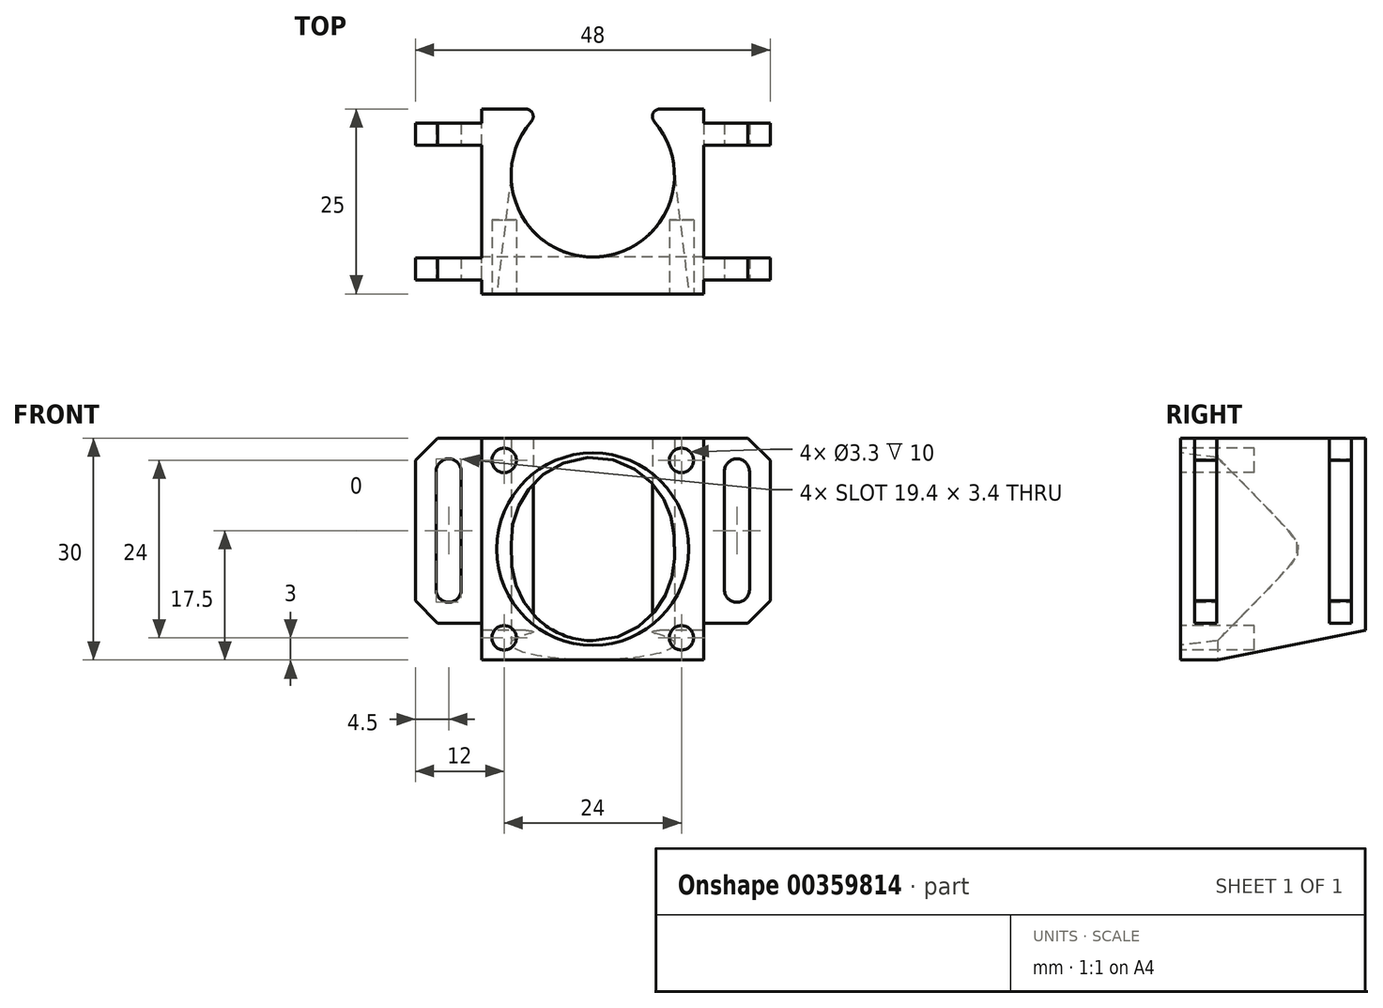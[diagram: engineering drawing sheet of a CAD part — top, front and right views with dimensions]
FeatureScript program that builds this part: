
annotation { "Feature Type Name" : "Feature", "Feature Type Description" : "" }
export const myFeature = defineFeature(function(context is Context, id is Id, definition is map)
    precondition{}
    {
        {
            var Q0;
            Q0=qCreatedBy(makeId("Top.planeOp"),FACE);
            var sketch = newSketch(context, id + "F0", { "sketchPlane" : qUnion([Q0])});
            skLineSegment(sketch, "E0.bottom", {"start": v(0, 0) * mm, "end": v(30, 0) * mm});
            skLineSegment(sketch, "E0.top", {"start": v(0, 25) * mm, "end": v(8.52, 25) * mm});
            skLineSegment(sketch, "E0.left", {"start": v(0, 0) * mm, "end": v(0, 25) * mm});
            skLineSegment(sketch, "E0.right", {"start": v(30, 0) * mm, "end": v(30, 25) * mm});
            skArc(sketch, "E1", {"start": v(8.52, 25) * mm, "mid": v(15, 5) * mm, "end": v(21.48, 25) * mm});
            skPoint(sketch, "E1.centerSnap0", {"position": v(15, 25) * mm});
            skLineSegment(sketch, "E2.trimOffspring", {"start": v(21.48, 25) * mm, "end": v(30, 25) * mm});
            skSolve(sketch);
        }
        {
            var Q0;
            Q0 = qSketchRegion(id + "F0", true);
            extrude(context, id + "F1", {"entities" : qUnion([Q0]), "depth" : 30 * mm});
        }
        {
            var Q0;
            Q0=makeQuery(id+"F1.opExtrude","SWEPT_FACE",FACE,{"disambiguationData":[OSD([sQuery(id+"F0.wireOp",EDGE,"E0.left")])]});
            var sketch = newSketch(context, id + "F2", { "sketchPlane" : qUnion([Q0])});
            skLineSegment(sketch, "E3", {"start": v(-25, 4) * mm, "end": v(-5, 0) * mm});
            skLineSegment(sketch, "E4", {"start": v(-5, 0) * mm, "end": v(-25, 0) * mm});
            skLineSegment(sketch, "E5", {"start": v(-25, 0) * mm, "end": v(-25, 4) * mm});
            skSolve(sketch);
        }
        {
            var Q0;
            Q0=makeQuery(id+"F2.imprint","IMPRINT",FACE,{"disambiguationData":[TD([[makeQuery(id+"F2.imprint","IMPRINT",EDGE,{"derivedFrom":sQuery(id+"F2.wireOp",EDGE,"E3")}),-1.0]])]});
            extrude(context, id + "F3", {"entities" : qUnion([Q0]), "operationType" : NewBodyOperationType.REMOVE, "endBound" : BoundingType.THROUGH_ALL, "oppositeDirection" : true, "depth" : 25 * mm});
        }
        {
            var Q0;
            Q0=makeQuery(id+"F1.opExtrude","CAP_FACE",FACE,{"disambiguationData":[OSD([sQuery(id+"F0.wireOp",EDGE,"E0.bottom"),sQuery(id+"F0.wireOp",EDGE,"E0.top"),sQuery(id+"F0.wireOp",EDGE,"E0.left"),sQuery(id+"F0.wireOp",EDGE,"E0.right"),sQuery(id+"F0.wireOp",EDGE,"E1"),sQuery(id+"F0.wireOp",EDGE,"E2.trimOffspring")])],"isStart":false});
            cPlane(context, id + "F4", {"entities" : qUnion([Q0]), "cplaneType" : CPlaneType.OFFSET, "offset" : 15 * mm, "oppositeDirection" : true, "width" : 150 * mm, "height" : 150 * mm});
        }
        {
            var Q0;
            Q0=qCreatedBy(id+"F4.planeOp",FACE);
            var sketch = newSketch(context, id + "F5", { "sketchPlane" : qUnion([Q0])});
            skArc(sketch, "E6.0.0", {"start": v(15, 5) * mm, "mid": v(7.19, 8.24) * mm, "end": v(3.95, 16.05) * mm});
            skLineSegment(sketch, "E6.0.1", {"start": v(8.52, 25) * mm, "end": v(0, 25) * mm, "construction": true});
            skLineSegment(sketch, "E6.0.2", {"start": v(0, 25) * mm, "end": v(0, 0) * mm, "construction": true});
            skLineSegment(sketch, "E6.0.3", {"start": v(0, 0) * mm, "end": v(30, 0) * mm, "construction": true});
            skLineSegment(sketch, "E6.0.4", {"start": v(30, 0) * mm, "end": v(30, 25) * mm, "construction": true});
            skLineSegment(sketch, "E6.0.5", {"start": v(30, 25) * mm, "end": v(21.48, 25) * mm, "construction": true});
            skLineSegment(sketch, "E7", {"start": v(3.95, 16.05) * mm, "end": v(2, 0) * mm});
            skLineSegment(sketch, "E8", {"start": v(2, 0) * mm, "end": v(15, 0) * mm});
            skLineSegment(sketch, "E9", {"start": v(15, 0) * mm, "end": v(15, 5) * mm});
            skLineSegment(sketch, "E10", {"start": v(15, 16.05) * mm, "end": v(15, 5) * mm, "construction": true});
            skSolve(sketch);
        }
        {
            var Q0;
            Q0 = qSketchRegion(id + "F5", true);
            var Q1;
            Q1=sQuery(id+"F5.wireOp",EDGE,"E10");
            revolve(context, id + "F6", {"operationType" : NewBodyOperationType.REMOVE, "entities" : qUnion([Q0]), "axis" : qUnion([Q1]), "revolveType" : RevolveType.FULL, "oppositeDirection" : true});
        }
        {
            var Q0;
            Q0=makeQuery(id+"F1.opExtrude","SWEPT_FACE",FACE,{"disambiguationData":[OSD([sQuery(id+"F0.wireOp",EDGE,"E0.bottom")])]});
            var sketch = newSketch(context, id + "F7", { "sketchPlane" : qUnion([Q0])});
            skCircle(sketch, "E11", {"center": v(3, 27) * mm, "radius": 1.65 * mm});
            skCircle(sketch, "E12", {"center": v(27, 27) * mm, "radius": 1.65 * mm});
            skCircle(sketch, "E13", {"center": v(27, 3) * mm, "radius": 1.65 * mm});
            skCircle(sketch, "E14", {"center": v(3, 3) * mm, "radius": 1.65 * mm});
            skSolve(sketch);
        }
        {
            var Q0;
            Q0 = qSketchRegion(id + "F7", true);
            extrude(context, id + "F8", {"entities" : qUnion([Q0]), "operationType" : NewBodyOperationType.REMOVE, "oppositeDirection" : true, "depth" : 10 * mm});
        }
        {
            var Q0;
            Q0=makeQuery(id+"F1.opExtrude","SWEPT_FACE",FACE,{"disambiguationData":[OSD([sQuery(id+"F0.wireOp",EDGE,"E0.right")])]});
            var sketch = newSketch(context, id + "F9", { "sketchPlane" : qUnion([Q0])});
            skLineSegment(sketch, "E15.bottom", {"start": v(1.9, 30) * mm, "end": v(4.9, 30) * mm});
            skLineSegment(sketch, "E15.top", {"start": v(1.9, 5) * mm, "end": v(4.9, 5) * mm});
            skLineSegment(sketch, "E15.left", {"start": v(1.9, 30) * mm, "end": v(1.9, 5) * mm});
            skLineSegment(sketch, "E15.right", {"start": v(4.9, 30) * mm, "end": v(4.9, 5) * mm});
            skLineSegment(sketch, "E16.bottom", {"start": v(23.1, 30) * mm, "end": v(20.1, 30) * mm});
            skLineSegment(sketch, "E16.top", {"start": v(23.1, 5) * mm, "end": v(20.1, 5) * mm});
            skLineSegment(sketch, "E16.left", {"start": v(23.1, 30) * mm, "end": v(23.1, 5) * mm});
            skLineSegment(sketch, "E16.right", {"start": v(20.1, 30) * mm, "end": v(20.1, 5) * mm});
            skSolve(sketch);
        }
        {
            var Q0;
            Q0=makeQuery(id+"F1.opExtrude","SWEPT_FACE",FACE,{"disambiguationData":[OSD([sQuery(id+"F0.wireOp",EDGE,"E0.left")])]});
            var sketch = newSketch(context, id + "F10", { "sketchPlane" : qUnion([Q0])});
            skLineSegment(sketch, "E17.0.0", {"start": v(-4.9, 5) * mm, "end": v(-4.9, 30) * mm});
            skLineSegment(sketch, "E17.0.1", {"start": v(-4.9, 30) * mm, "end": v(-1.9, 30) * mm});
            skLineSegment(sketch, "E17.0.2", {"start": v(-1.9, 30) * mm, "end": v(-1.9, 5) * mm});
            skLineSegment(sketch, "E17.0.3", {"start": v(-1.9, 5) * mm, "end": v(-4.9, 5) * mm});
            skLineSegment(sketch, "E18.0.0", {"start": v(-23.1, 30) * mm, "end": v(-20.1, 30) * mm});
            skLineSegment(sketch, "E18.0.1", {"start": v(-20.1, 30) * mm, "end": v(-20.1, 5) * mm});
            skLineSegment(sketch, "E18.0.2", {"start": v(-20.1, 5) * mm, "end": v(-23.1, 5) * mm});
            skLineSegment(sketch, "E18.0.3", {"start": v(-23.1, 5) * mm, "end": v(-23.1, 30) * mm});
            skSolve(sketch);
        }
        {
            var Q0;
            Q0 = qSketchRegion(id + "F9", true);
            extrude(context, id + "F11", {"entities" : qUnion([Q0]), "operationType" : NewBodyOperationType.ADD, "depth" : 9 * mm});
        }
        {
            var Q0;
            Q0 = qSketchRegion(id + "F10", true);
            extrude(context, id + "F12", {"entities" : qUnion([Q0]), "operationType" : NewBodyOperationType.ADD, "depth" : 9 * mm});
        }
        {
            var Q0;
            Q0=makeQuery(id+"F12.opExtrude","SWEPT_FACE",FACE,{"disambiguationData":[OSD([sQuery(id+"F10.wireOp",EDGE,"E17.0.2")])]});
            var sketch = newSketch(context, id + "F13", { "sketchPlane" : qUnion([Q0])});
            skLineSegment(sketch, "E19.0", {"start": v(-2.8, 7.8) * mm, "end": v(-2.8, 27.2) * mm});
            skLineSegment(sketch, "E19.1", {"start": v(-6.2, 7.8) * mm, "end": v(-2.8, 7.8) * mm});
            skLineSegment(sketch, "E19.2", {"start": v(-6.2, 27.2) * mm, "end": v(-6.2, 7.8) * mm});
            skLineSegment(sketch, "E19.3", {"start": v(-2.8, 27.2) * mm, "end": v(-6.2, 27.2) * mm});
            skLineSegment(sketch, "E20.0", {"start": v(32.8, 27.2) * mm, "end": v(32.8, 7.8) * mm});
            skLineSegment(sketch, "E20.1", {"start": v(36.2, 27.2) * mm, "end": v(32.8, 27.2) * mm});
            skLineSegment(sketch, "E20.2", {"start": v(36.2, 7.8) * mm, "end": v(36.2, 27.2) * mm});
            skLineSegment(sketch, "E20.3", {"start": v(32.8, 7.8) * mm, "end": v(36.2, 7.8) * mm});
            skSolve(sketch);
        }
        {
            var Q0;
            Q0 = qSketchRegion(id + "F13", true);
            extrude(context, id + "F14", {"entities" : qUnion([Q0]), "operationType" : NewBodyOperationType.REMOVE, "endBound" : BoundingType.THROUGH_ALL, "oppositeDirection" : true, "depth" : 25 * mm});
        }
        {
            var Q0;
            {var subQ0=sQuery(id+"F13.wireOp",EDGE,"E19.0");var subQ1=sQuery(id+"F13.wireOp",EDGE,"E19.3");Q0=makeQuery(id+"F14.boolean.opBoolean","COPY",EDGE,{"disambiguationData":[TD([makeQuery(id+"F12.opExtrude","SWEPT_FACE",FACE,{"disambiguationData":[OSD([sQuery(id+"F10.wireOp",EDGE,"E17.0.0")])]})])],"derivedFrom":makeQuery(id+"F14.opExtrude","SWEPT_EDGE",EDGE,{"disambiguationData":[OSD([subQ0,subQ1])]})});}
            var Q1;
            {var subQ0=sQuery(id+"F13.wireOp",EDGE,"E19.3");var subQ1=sQuery(id+"F13.wireOp",EDGE,"E19.2");Q1=makeQuery(id+"F14.boolean.opBoolean","COPY",EDGE,{"disambiguationData":[TD([makeQuery(id+"F12.opExtrude","SWEPT_FACE",FACE,{"disambiguationData":[OSD([sQuery(id+"F10.wireOp",EDGE,"E17.0.0")])]})])],"derivedFrom":makeQuery(id+"F14.opExtrude","SWEPT_EDGE",EDGE,{"disambiguationData":[OSD([subQ1,subQ0])]})});}
            var Q2;
            {var subQ0=sQuery(id+"F13.wireOp",EDGE,"E19.1");var subQ1=sQuery(id+"F13.wireOp",EDGE,"E19.2");Q2=makeQuery(id+"F14.boolean.opBoolean","COPY",EDGE,{"disambiguationData":[TD([makeQuery(id+"F12.opExtrude","SWEPT_FACE",FACE,{"disambiguationData":[OSD([sQuery(id+"F10.wireOp",EDGE,"E17.0.0")])]})])],"derivedFrom":makeQuery(id+"F14.opExtrude","SWEPT_EDGE",EDGE,{"disambiguationData":[OSD([subQ0,subQ1])]})});}
            var Q3;
            {var subQ0=sQuery(id+"F13.wireOp",EDGE,"E19.1");var subQ1=sQuery(id+"F13.wireOp",EDGE,"E19.2");Q3=makeQuery(id+"F14.boolean.opBoolean","COPY",EDGE,{"disambiguationData":[TD([makeQuery(id+"F12.opExtrude","SWEPT_FACE",FACE,{"disambiguationData":[OSD([sQuery(id+"F10.wireOp",EDGE,"E18.0.1")])]})])],"derivedFrom":makeQuery(id+"F14.opExtrude","SWEPT_EDGE",EDGE,{"disambiguationData":[OSD([subQ0,subQ1])]})});}
            var Q4;
            {var subQ0=sQuery(id+"F13.wireOp",EDGE,"E20.0");var subQ1=sQuery(id+"F13.wireOp",EDGE,"E20.3");Q4=makeQuery(id+"F14.boolean.opBoolean","COPY",EDGE,{"disambiguationData":[TD([makeQuery(id+"F11.opExtrude","SWEPT_FACE",FACE,{"disambiguationData":[OSD([sQuery(id+"F9.wireOp",EDGE,"E16.left")])]})])],"derivedFrom":makeQuery(id+"F14.opExtrude","SWEPT_EDGE",EDGE,{"disambiguationData":[OSD([subQ0,subQ1])]})});}
            var Q5;
            {var subQ0=sQuery(id+"F13.wireOp",EDGE,"E20.0");var subQ1=sQuery(id+"F13.wireOp",EDGE,"E20.3");Q5=makeQuery(id+"F14.boolean.opBoolean","COPY",EDGE,{"disambiguationData":[TD([makeQuery(id+"F11.opExtrude","SWEPT_FACE",FACE,{"disambiguationData":[OSD([sQuery(id+"F9.wireOp",EDGE,"E15.left")])]})])],"derivedFrom":makeQuery(id+"F14.opExtrude","SWEPT_EDGE",EDGE,{"disambiguationData":[OSD([subQ0,subQ1])]})});}
            var Q6;
            {var subQ0=sQuery(id+"F13.wireOp",EDGE,"E20.1");var subQ1=sQuery(id+"F13.wireOp",EDGE,"E20.2");Q6=makeQuery(id+"F14.boolean.opBoolean","COPY",EDGE,{"disambiguationData":[TD([makeQuery(id+"F11.opExtrude","SWEPT_FACE",FACE,{"disambiguationData":[OSD([sQuery(id+"F9.wireOp",EDGE,"E15.left")])]})])],"derivedFrom":makeQuery(id+"F14.opExtrude","SWEPT_EDGE",EDGE,{"disambiguationData":[OSD([subQ0,subQ1])]})});}
            var Q7;
            {var subQ0=sQuery(id+"F13.wireOp",EDGE,"E20.1");var subQ1=sQuery(id+"F13.wireOp",EDGE,"E20.0");Q7=makeQuery(id+"F14.boolean.opBoolean","COPY",EDGE,{"disambiguationData":[TD([makeQuery(id+"F11.opExtrude","SWEPT_FACE",FACE,{"disambiguationData":[OSD([sQuery(id+"F9.wireOp",EDGE,"E16.left")])]})])],"derivedFrom":makeQuery(id+"F14.opExtrude","SWEPT_EDGE",EDGE,{"disambiguationData":[OSD([subQ1,subQ0])]})});}
            var Q8;
            {var subQ0=sQuery(id+"F13.wireOp",EDGE,"E20.1");var subQ1=sQuery(id+"F13.wireOp",EDGE,"E20.0");Q8=makeQuery(id+"F14.boolean.opBoolean","COPY",EDGE,{"disambiguationData":[TD([makeQuery(id+"F11.opExtrude","SWEPT_FACE",FACE,{"disambiguationData":[OSD([sQuery(id+"F9.wireOp",EDGE,"E15.left")])]})])],"derivedFrom":makeQuery(id+"F14.opExtrude","SWEPT_EDGE",EDGE,{"disambiguationData":[OSD([subQ1,subQ0])]})});}
            var Q9;
            {var subQ0=sQuery(id+"F13.wireOp",EDGE,"E20.2");var subQ1=sQuery(id+"F13.wireOp",EDGE,"E20.3");Q9=makeQuery(id+"F14.boolean.opBoolean","COPY",EDGE,{"disambiguationData":[TD([makeQuery(id+"F11.opExtrude","SWEPT_FACE",FACE,{"disambiguationData":[OSD([sQuery(id+"F9.wireOp",EDGE,"E16.left")])]})])],"derivedFrom":makeQuery(id+"F14.opExtrude","SWEPT_EDGE",EDGE,{"disambiguationData":[OSD([subQ0,subQ1])]})});}
            var Q10;
            {var subQ0=sQuery(id+"F13.wireOp",EDGE,"E20.2");var subQ1=sQuery(id+"F13.wireOp",EDGE,"E20.3");Q10=makeQuery(id+"F14.boolean.opBoolean","COPY",EDGE,{"disambiguationData":[TD([makeQuery(id+"F11.opExtrude","SWEPT_FACE",FACE,{"disambiguationData":[OSD([sQuery(id+"F9.wireOp",EDGE,"E15.left")])]})])],"derivedFrom":makeQuery(id+"F14.opExtrude","SWEPT_EDGE",EDGE,{"disambiguationData":[OSD([subQ0,subQ1])]})});}
            var Q11;
            {var subQ0=sQuery(id+"F13.wireOp",EDGE,"E19.0");var subQ1=sQuery(id+"F13.wireOp",EDGE,"E19.1");Q11=makeQuery(id+"F14.boolean.opBoolean","COPY",EDGE,{"disambiguationData":[TD([makeQuery(id+"F12.opExtrude","SWEPT_FACE",FACE,{"disambiguationData":[OSD([sQuery(id+"F10.wireOp",EDGE,"E18.0.1")])]})])],"derivedFrom":makeQuery(id+"F14.opExtrude","SWEPT_EDGE",EDGE,{"disambiguationData":[OSD([subQ0,subQ1])]})});}
            var Q12;
            {var subQ0=sQuery(id+"F13.wireOp",EDGE,"E19.0");var subQ1=sQuery(id+"F13.wireOp",EDGE,"E19.1");Q12=makeQuery(id+"F14.boolean.opBoolean","COPY",EDGE,{"disambiguationData":[TD([makeQuery(id+"F12.opExtrude","SWEPT_FACE",FACE,{"disambiguationData":[OSD([sQuery(id+"F10.wireOp",EDGE,"E17.0.0")])]})])],"derivedFrom":makeQuery(id+"F14.opExtrude","SWEPT_EDGE",EDGE,{"disambiguationData":[OSD([subQ0,subQ1])]})});}
            var Q13;
            {var subQ0=sQuery(id+"F13.wireOp",EDGE,"E19.0");var subQ1=sQuery(id+"F13.wireOp",EDGE,"E19.3");Q13=makeQuery(id+"F14.boolean.opBoolean","COPY",EDGE,{"disambiguationData":[TD([makeQuery(id+"F12.opExtrude","SWEPT_FACE",FACE,{"disambiguationData":[OSD([sQuery(id+"F10.wireOp",EDGE,"E18.0.1")])]})])],"derivedFrom":makeQuery(id+"F14.opExtrude","SWEPT_EDGE",EDGE,{"disambiguationData":[OSD([subQ0,subQ1])]})});}
            var Q14;
            {var subQ0=sQuery(id+"F13.wireOp",EDGE,"E19.3");var subQ1=sQuery(id+"F13.wireOp",EDGE,"E19.2");Q14=makeQuery(id+"F14.boolean.opBoolean","COPY",EDGE,{"disambiguationData":[TD([makeQuery(id+"F12.opExtrude","SWEPT_FACE",FACE,{"disambiguationData":[OSD([sQuery(id+"F10.wireOp",EDGE,"E18.0.1")])]})])],"derivedFrom":makeQuery(id+"F14.opExtrude","SWEPT_EDGE",EDGE,{"disambiguationData":[OSD([subQ1,subQ0])]})});}
            var Q15;
            {var subQ0=sQuery(id+"F13.wireOp",EDGE,"E20.1");var subQ1=sQuery(id+"F13.wireOp",EDGE,"E20.2");Q15=makeQuery(id+"F14.boolean.opBoolean","COPY",EDGE,{"disambiguationData":[TD([makeQuery(id+"F11.opExtrude","SWEPT_FACE",FACE,{"disambiguationData":[OSD([sQuery(id+"F9.wireOp",EDGE,"E16.left")])]})])],"derivedFrom":makeQuery(id+"F14.opExtrude","SWEPT_EDGE",EDGE,{"disambiguationData":[OSD([subQ0,subQ1])]})});}
            fillet(context, id + "F15", {"entities" : qUnion([Q0, Q1, Q2, Q3, Q4, Q5, Q6, Q7, Q8, Q9, Q10, Q11, Q12, Q13, Q14, Q15]), "radius" : 1.7 * mm, "tangentPropagation" : true, "allowEdgeOverflow" : false});
        }
        {
            var Q0;
            Q0=makeQuery(id+"F1.opExtrude","SWEPT_EDGE",EDGE,{"disambiguationData":[OSD([sQuery(id+"F0.wireOp",EDGE,"E0.top"),sQuery(id+"F0.wireOp",EDGE,"E1")])]});
            var Q1;
            Q1=makeQuery(id+"F1.opExtrude","SWEPT_EDGE",EDGE,{"disambiguationData":[OSD([sQuery(id+"F0.wireOp",EDGE,"E1"),sQuery(id+"F0.wireOp",EDGE,"E2.trimOffspring")])]});
            fillet(context, id + "F16", {"entities" : qUnion([Q0, Q1]), "radius" : 1 * mm, "tangentPropagation" : true, "allowEdgeOverflow" : false});
        }
        {
            var Q0;
            Q0=makeQuery(id+"F12.opExtrude","CAP_EDGE",EDGE,{"disambiguationData":[OSD([sQuery(id+"F10.wireOp",EDGE,"E18.0.0")])],"isStart":false});
            var Q1;
            Q1=makeQuery(id+"F12.opExtrude","CAP_EDGE",EDGE,{"disambiguationData":[OSD([sQuery(id+"F10.wireOp",EDGE,"E18.0.2")])],"isStart":false});
            var Q2;
            Q2=makeQuery(id+"F12.opExtrude","CAP_EDGE",EDGE,{"disambiguationData":[OSD([sQuery(id+"F10.wireOp",EDGE,"E17.0.3")])],"isStart":false});
            var Q3;
            Q3=makeQuery(id+"F12.opExtrude","CAP_EDGE",EDGE,{"disambiguationData":[OSD([sQuery(id+"F10.wireOp",EDGE,"E17.0.1")])],"isStart":false});
            var Q4;
            Q4=makeQuery(id+"F11.opExtrude","CAP_EDGE",EDGE,{"disambiguationData":[OSD([sQuery(id+"F9.wireOp",EDGE,"E15.bottom")])],"isStart":false});
            var Q5;
            Q5=makeQuery(id+"F11.opExtrude","CAP_EDGE",EDGE,{"disambiguationData":[OSD([sQuery(id+"F9.wireOp",EDGE,"E16.bottom")])],"isStart":false});
            var Q6;
            Q6=makeQuery(id+"F11.opExtrude","CAP_EDGE",EDGE,{"disambiguationData":[OSD([sQuery(id+"F9.wireOp",EDGE,"E16.top")])],"isStart":false});
            var Q7;
            Q7=makeQuery(id+"F11.opExtrude","CAP_EDGE",EDGE,{"disambiguationData":[OSD([sQuery(id+"F9.wireOp",EDGE,"E15.top")])],"isStart":false});
            chamfer(context, id + "F17", {"entities" : qUnion([Q0, Q1, Q2, Q3, Q4, Q5, Q6, Q7]), "width" : 3 * mm, "tangentPropagation" : true});
        }
    });
